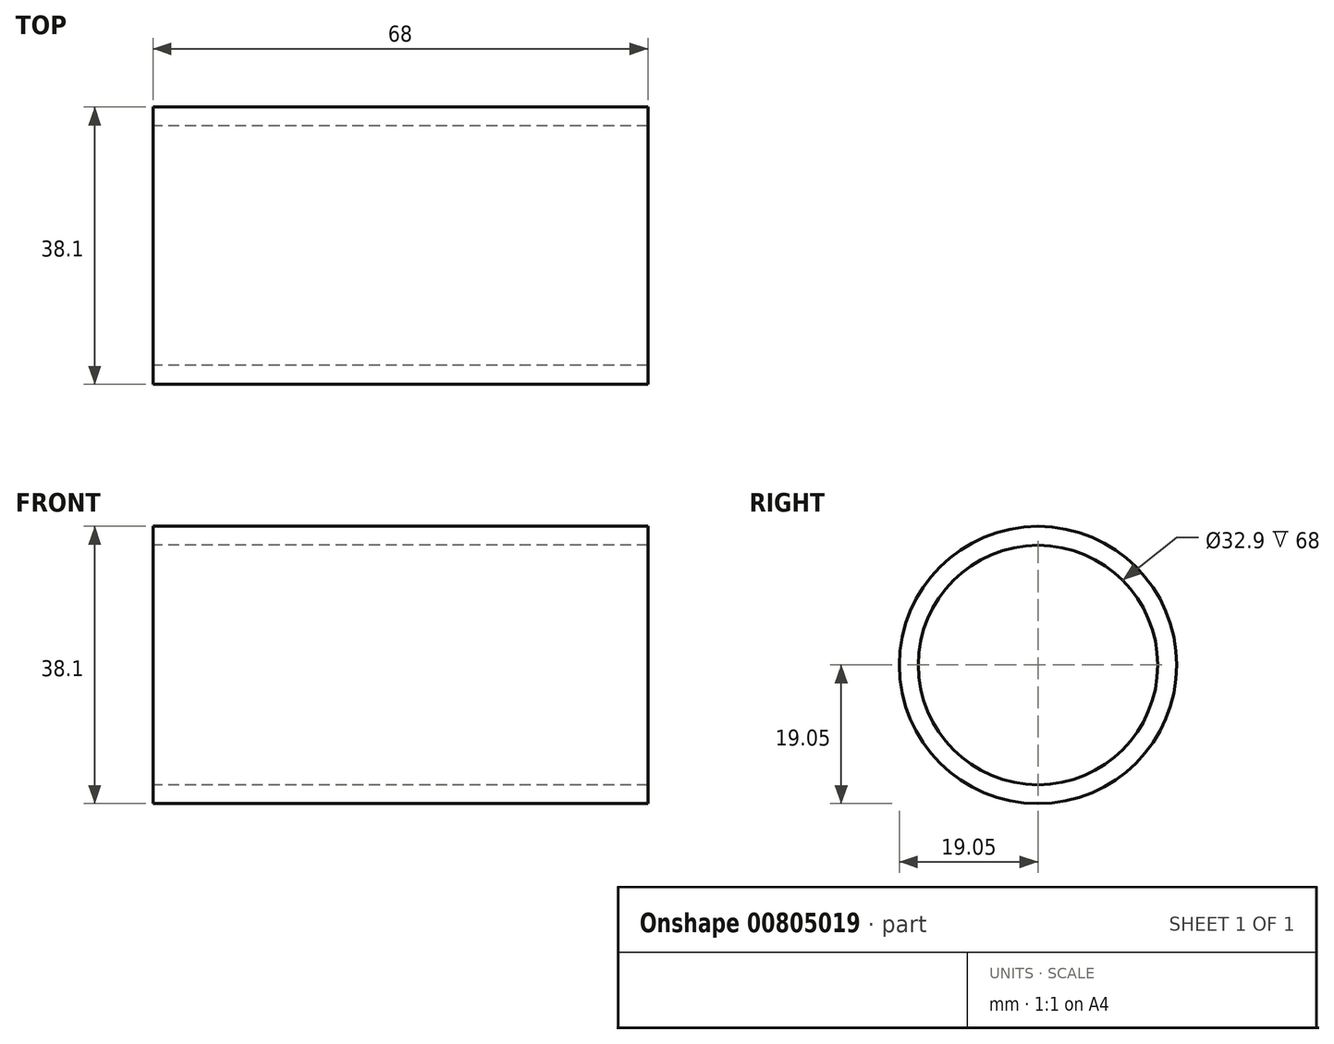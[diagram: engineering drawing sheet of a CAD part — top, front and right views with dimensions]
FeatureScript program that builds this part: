
annotation { "Feature Type Name" : "Feature", "Feature Type Description" : "" }
export const myFeature = defineFeature(function(context is Context, id is Id, definition is map)
    precondition{}
    {
        {
            var Q0;
            Q0=qCreatedBy(makeId("Right.planeOp"),FACE);
            var sketch = newSketch(context, id + "F0", { "sketchPlane" : qUnion([Q0])});
            skCircle(sketch, "E0", {"center": v(0, 0) * mm, "radius": 19.05 * mm});
            skCircle(sketch, "E1", {"center": v(0, 0) * mm, "radius": 16.45 * mm});
            skSolve(sketch);
        }
        {
            var Q0;
            Q0=makeQuery(id+"F0.imprint","IMPRINT",FACE,{"disambiguationData":[TD([[makeQuery(id+"F0.imprint","IMPRINT",EDGE,{"derivedFrom":sQuery(id+"F0.wireOp",EDGE,"E0")}),1.0]])]});
            extrude(context, id + "F1", {"entities" : qUnion([Q0]), "endBound" : BoundingType.SYMMETRIC, "depth" : 68 * mm, "offsetDistance" : 25.4 * mm});
        }
    });
